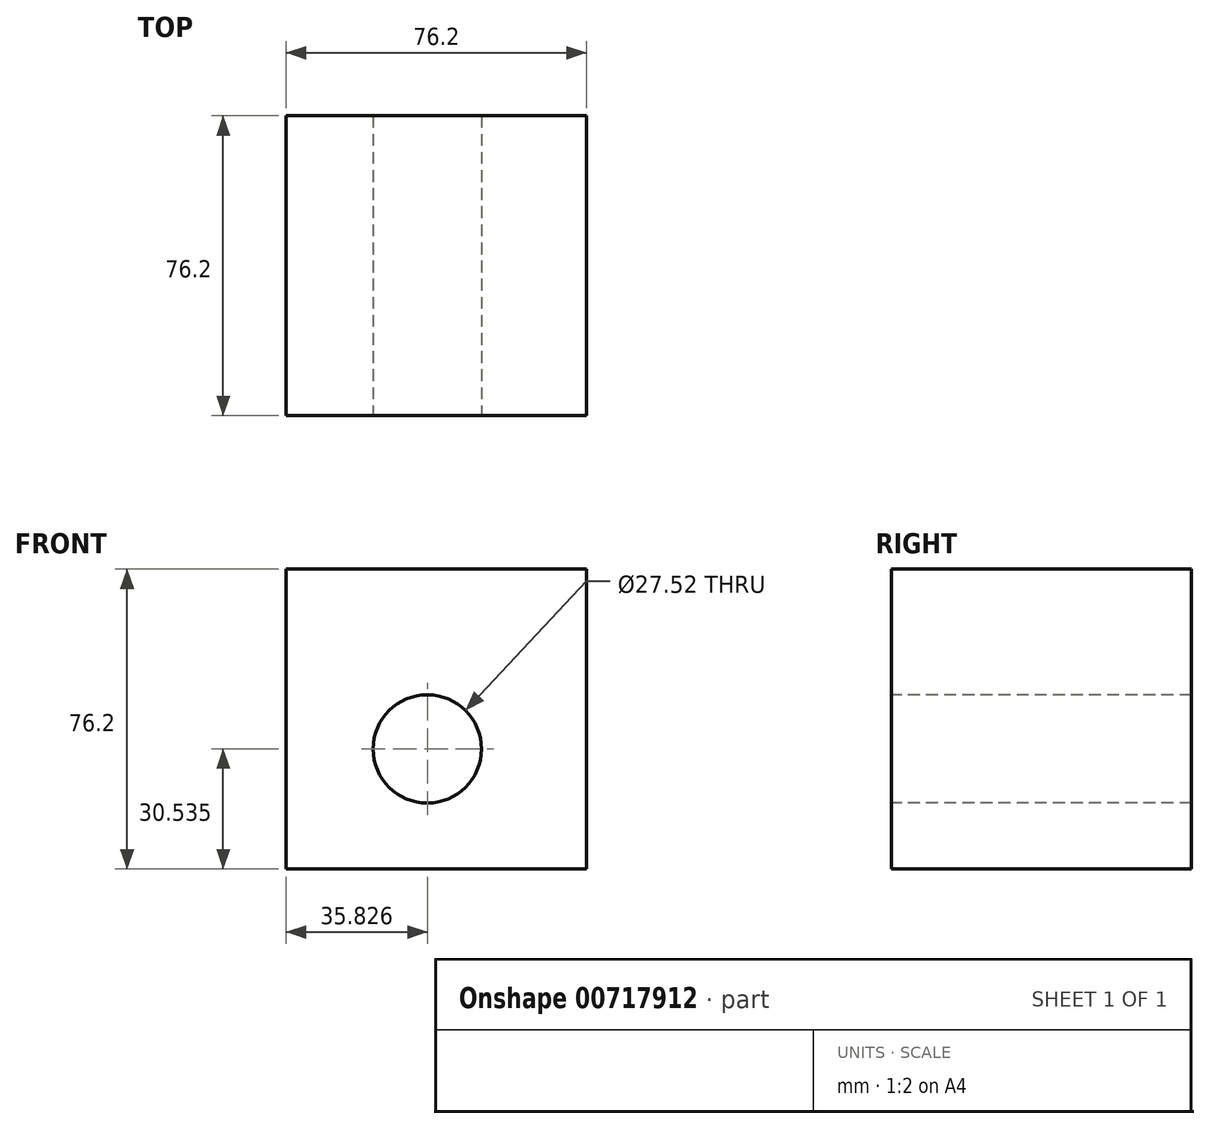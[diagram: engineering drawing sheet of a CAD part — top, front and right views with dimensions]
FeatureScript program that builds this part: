
annotation { "Feature Type Name" : "Feature", "Feature Type Description" : "" }
export const myFeature = defineFeature(function(context is Context, id is Id, definition is map)
    precondition{}
    {
        {
            var Q0;
            Q0=qCreatedBy(makeId("Front.planeOp"),FACE);
            var sketch = newSketch(context, id + "F0", { "sketchPlane" : qUnion([Q0])});
            skLineSegment(sketch, "E0.bottom", {"start": v(-25.15, 26.08) * mm, "end": v(51.05, 26.08) * mm});
            skLineSegment(sketch, "E0.top", {"start": v(-25.15, -50.12) * mm, "end": v(51.05, -50.12) * mm});
            skLineSegment(sketch, "E0.left", {"start": v(-25.15, 26.08) * mm, "end": v(-25.15, -50.12) * mm});
            skLineSegment(sketch, "E0.right", {"start": v(51.05, 26.08) * mm, "end": v(51.05, -50.12) * mm});
            skSolve(sketch);
        }
        {
            var Q0;
            Q0=makeQuery(id+"F0.imprint","IMPRINT",FACE,{"disambiguationData":[TD([[makeQuery(id+"F0.imprint","IMPRINT",EDGE,{"derivedFrom":sQuery(id+"F0.wireOp",EDGE,"E0.bottom")}),-1.0]])]});
            extrude(context, id + "F1", {"entities" : qUnion([Q0]), "endBound" : BoundingType.SYMMETRIC, "depth" : 76.2 * mm, "offsetDistance" : 25.4 * mm});
        }
        {
            var Q0;
            Q0=makeQuery(id+"F1.opExtrude","CAP_FACE",FACE,{"disambiguationData":[OSD([sQuery(id+"F0.wireOp",EDGE,"E0.bottom"),sQuery(id+"F0.wireOp",EDGE,"E0.top"),sQuery(id+"F0.wireOp",EDGE,"E0.left"),sQuery(id+"F0.wireOp",EDGE,"E0.right")])],"isStart":false});
            var sketch = newSketch(context, id + "F2", { "sketchPlane" : qUnion([Q0])});
            skCircle(sketch, "E1", {"center": v(10.68, -19.58) * mm, "radius": 13.76 * mm});
            skSolve(sketch);
        }
        {
            var Q0;
            Q0 = qSketchRegion(id + "F2", true);
            extrude(context, id + "F3", {"entities" : qUnion([Q0]), "operationType" : NewBodyOperationType.REMOVE, "endBound" : BoundingType.THROUGH_ALL, "oppositeDirection" : true, "depth" : 25.4 * mm, "offsetDistance" : 25.4 * mm});
        }
    });
